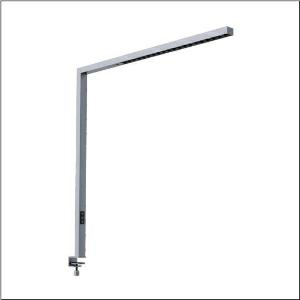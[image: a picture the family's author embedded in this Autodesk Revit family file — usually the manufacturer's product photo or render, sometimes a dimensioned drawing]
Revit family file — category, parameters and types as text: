
# Revit family: silica_r__31_desk_51my52gatcs_8ab4
name_source: partatom
category: Lighting Fixtures
units: mm (PartAtom-declared; Revit-internal decimal feet)

## family parameters
Cut with Voids When Loaded = No
Host = Face
Light Source = No
Part Type = Normal
Room Calculation Point = No
Round Connector Dimension = Use Diameter
Shared = No

## types (1)
- --- (1 x LED, 8520 lm, 71 W, 4000K)
    Apparent Load = 71 VA
    CIE Flux Codes = 86 100 100 24 100
    Color Rendering = 80
    Color Temperature = 4000K
    Default Elevation = 1800 mm
    Description = Silica® 31 Desk, desktop luminaire, secondary optical cover: cover panel, of PMMA, light emission: direct/indirect distribution, primary light characteristic: symmetric, installation type: as desk luminaire, LED, rated luminous flux: 8.520lm, luminous efficacy: 120lm/W, light colour: 8tw, colour temperature: 2700..6500K, daylight-dependent control, with cable with plug, mains connection: 230V, AC, 50Hz, connection cable pre-assembled, rated input power: 71W, luminaire head, of aluminium, metallic grey (RAL 9006), length: 1.203mm, width: 52mm, supporting column, angular, of aluminium, metallic grey (RAL 9006), baseplate, of steel, metallic grey (RAL 9006), protection rating (complete): IP20, insulation class (complete): insulation class I (protective earthing), certification: CE, permissible operating ambient temperature: -20..+40°C, standard: EN 50419, packaging unit: 1 piece
    Height = 36 mm
    Lamp = 1 x LED
    Lamp Light Flux = 8520 lm
    Lamp Power = 71 W
    Lamp count = 1
    Length = 1203 mm
    Luminous efficacy = 120 lm/W
    Manufacturer = Siteco
    ModVariant = No
    Model = 51MY52GATCS
    Mounting Place = Floor
    Mounting Type = Freestanding
    Number of Poles = 1
    OnlyDefault = Yes
    Power Factor = 1
    Product Name = Silica® 31 Desk
    Product group = desktop luminaire
    ProductGroupID = 1302
    Protection Class = Protection class I
    Protection Degree = IP 20
    RLX_Detail_Level = 1
    RLX_Emergency_Light_Flux = 0 lm
    RLX_Emergency_Type = 0
    RLX_Emergency_Type_DB = No
    RlxData = <blob elided: 19601 chars, md5=21163f49>
    Socket = socket
    Standby Power = 0 W
    System Light Flux = 8520 lm
    System Power = 71 W
    Type Comments = factory setting
    Type Image = l_1275333.jpg
    URL = http://relux.com
    VarID = @adj_032431
    Voltage = 0 V
    Weight = 0.00 kg
    Width = 52 mm  [stored 0.170604 ft]

note: [stored X ft] marks values corroborated as IEEE doubles in the binary element streams (Revit-internal decimal feet)

## geometry (parser evidence)
native form markers: Blend x4, Sweep x15
no freeform markers — native parametric forms only
